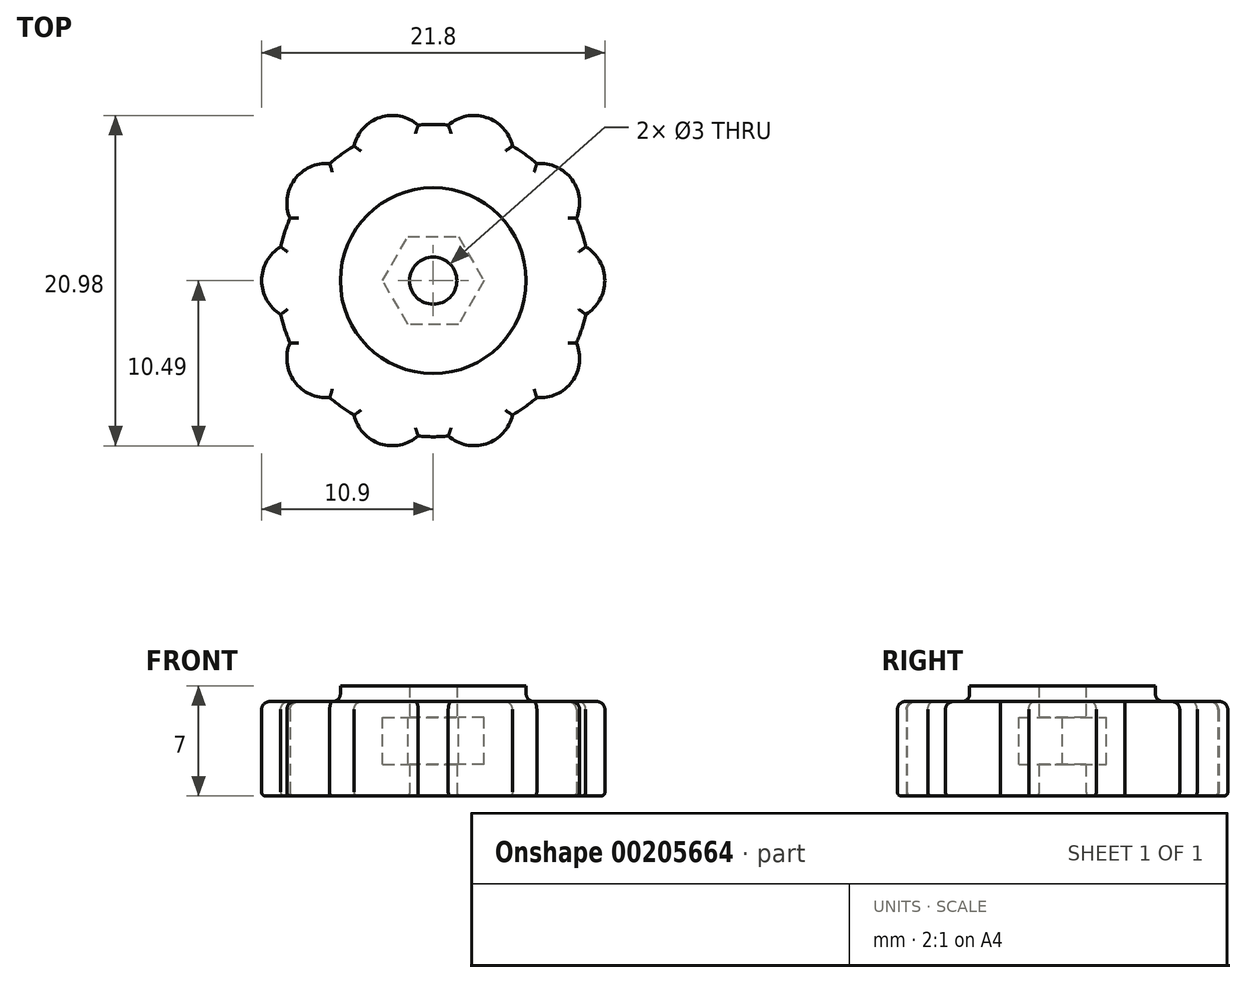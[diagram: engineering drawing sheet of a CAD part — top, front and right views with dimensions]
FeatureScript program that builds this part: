
annotation { "Feature Type Name" : "Feature", "Feature Type Description" : "" }
export const myFeature = defineFeature(function(context is Context, id is Id, definition is map)
    precondition{}
    {
        {
            var Q0;
            Q0=qCreatedBy(makeId("Top.planeOp"),FACE);
            var sketch = newSketch(context, id + "F0", { "sketchPlane" : qUnion([Q0])});
            skArc(sketch, "E0", {"start": v(-1.29, 2.14) * mm, "mid": v(-2.5, 0) * mm, "end": v(-1.29, -2.14) * mm});
            skArc(sketch, "E1.1.0", {"start": v(-0.7, -3.96) * mm, "mid": v(-0.42, -6.4) * mm, "end": v(1.82, -7.43) * mm});
            skArc(sketch, "E1.2.0", {"start": v(3.37, -8.55) * mm, "mid": v(5.03, -10.37) * mm, "end": v(7.45, -9.87) * mm});
            skArc(sketch, "E1.3.0", {"start": v(9.35, -9.87) * mm, "mid": v(11.77, -10.37) * mm, "end": v(13.43, -8.55) * mm});
            skArc(sketch, "E1.4.0", {"start": v(14.98, -7.43) * mm, "mid": v(17.22, -6.4) * mm, "end": v(17.5, -3.96) * mm});
            skArc(sketch, "E1.5.0", {"start": v(18.09, -2.14) * mm, "mid": v(19.3, 0) * mm, "end": v(18.09, 2.14) * mm});
            skArc(sketch, "E1.6.0", {"start": v(17.5, 3.96) * mm, "mid": v(17.22, 6.4) * mm, "end": v(14.98, 7.43) * mm});
            skArc(sketch, "E1.7.0", {"start": v(13.43, 8.55) * mm, "mid": v(11.77, 10.37) * mm, "end": v(9.35, 9.87) * mm});
            skArc(sketch, "E1.8.0", {"start": v(7.45, 9.87) * mm, "mid": v(5.03, 10.37) * mm, "end": v(3.37, 8.55) * mm});
            skArc(sketch, "E1.9.0", {"start": v(1.82, 7.43) * mm, "mid": v(-0.42, 6.4) * mm, "end": v(-0.7, 3.96) * mm});
            skPoint(sketch, "E1.center", {"position": v(8.4, 0) * mm});
            skArc(sketch, "E2", {"start": v(3.37, 8.55) * mm, "mid": v(2.57, 8.03) * mm, "end": v(1.82, 7.43) * mm});
            skCircle(sketch, "E3.cCircle", {"center": v(8.4, 0) * mm, "radius": 2.75 * mm, "construction": true});
            skLineSegment(sketch, "E3.0", {"start": v(9.99, -2.75) * mm, "end": v(6.81, -2.75) * mm});
            skLineSegment(sketch, "E3.1", {"start": v(6.81, -2.75) * mm, "end": v(5.22, 0) * mm});
            skLineSegment(sketch, "E3.2", {"start": v(5.22, 0) * mm, "end": v(6.81, 2.75) * mm});
            skLineSegment(sketch, "E3.3", {"start": v(6.81, 2.75) * mm, "end": v(9.99, 2.75) * mm});
            skLineSegment(sketch, "E3.4", {"start": v(9.99, 2.75) * mm, "end": v(11.58, 0) * mm});
            skLineSegment(sketch, "E3.5", {"start": v(11.58, 0) * mm, "end": v(9.99, -2.75) * mm});
            skPoint(sketch, "E3.0.midPoint", {"position": v(8.4, -2.75) * mm});
            skCircle(sketch, "E4", {"center": v(8.4, 0) * mm, "radius": 5.9 * mm});
            skArc(sketch, "E5.trimOffspring", {"start": v(-0.7, 3.96) * mm, "mid": v(-1.03, 3.07) * mm, "end": v(-1.29, 2.14) * mm});
            skArc(sketch, "E6.trimOffspring", {"start": v(-1.29, -2.14) * mm, "mid": v(-1.03, -3.07) * mm, "end": v(-0.7, -3.96) * mm});
            skArc(sketch, "E7.trimOffspring", {"start": v(1.82, -7.43) * mm, "mid": v(2.57, -8.03) * mm, "end": v(3.37, -8.55) * mm});
            skArc(sketch, "E8.trimOffspring", {"start": v(7.45, -9.87) * mm, "mid": v(8.4, -9.92) * mm, "end": v(9.35, -9.87) * mm});
            skArc(sketch, "E9.trimOffspring", {"start": v(17.5, -3.96) * mm, "mid": v(17.83, -3.07) * mm, "end": v(18.09, -2.14) * mm});
            skArc(sketch, "E10.trimOffspring", {"start": v(13.43, -8.55) * mm, "mid": v(14.23, -8.03) * mm, "end": v(14.98, -7.43) * mm});
            skArc(sketch, "E11.trimOffspring", {"start": v(18.09, 2.14) * mm, "mid": v(17.83, 3.07) * mm, "end": v(17.5, 3.96) * mm});
            skArc(sketch, "E12.trimOffspring", {"start": v(14.98, 7.43) * mm, "mid": v(14.23, 8.03) * mm, "end": v(13.43, 8.55) * mm});
            skArc(sketch, "E13.trimOffspring", {"start": v(9.35, 9.87) * mm, "mid": v(8.4, 9.92) * mm, "end": v(7.45, 9.87) * mm});
            skCircle(sketch, "E14", {"center": v(8.4, 0) * mm, "radius": 1.5 * mm});
            skSolve(sketch);
        }
        {
            var Q0;
            Q0=makeQuery(id+"F0.imprint","IMPRINT",FACE,{"disambiguationData":[TD([[makeQuery(id+"F0.imprint","IMPRINT",EDGE,{"derivedFrom":sQuery(id+"F0.wireOp",EDGE,"E0")}),1.0]])]});
            var Q1;
            Q1=makeQuery(id+"F0.imprint","IMPRINT",FACE,{"disambiguationData":[TD([[makeQuery(id+"F0.imprint","IMPRINT",EDGE,{"derivedFrom":sQuery(id+"F0.wireOp",EDGE,"E3.0")}),1.0]])]});
            var Q2;
            Q2=makeQuery(id+"F0.imprint","IMPRINT",FACE,{"disambiguationData":[TD([[makeQuery(id+"F0.imprint","IMPRINT",EDGE,{"derivedFrom":sQuery(id+"F0.wireOp",EDGE,"E3.0")}),-1.0]])]});
            extrude(context, id + "F1", {"entities" : qUnion([Q0, Q1, Q2]), "depth" : 6 * mm});
        }
        {
            var Q0;
            Q0=makeQuery(id+"F0.imprint","IMPRINT",FACE,{"disambiguationData":[TD([[makeQuery(id+"F0.imprint","IMPRINT",EDGE,{"derivedFrom":sQuery(id+"F0.wireOp",EDGE,"E3.0")}),1.0]])]});
            extrude(context, id + "F2", {"entities" : qUnion([Q0]), "operationType" : NewBodyOperationType.ADD, "depth" : 7 * mm});
        }
        {
            var Q0;
            Q0=makeQuery(id+"F0.imprint","IMPRINT",FACE,{"disambiguationData":[TD([[makeQuery(id+"F0.imprint","IMPRINT",EDGE,{"derivedFrom":sQuery(id+"F0.wireOp",EDGE,"E3.0")}),-1.0]])]});
            extrude(context, id + "F3", {"entities" : qUnion([Q0]), "operationType" : NewBodyOperationType.ADD, "depth" : 7 * mm});
        }
        {
            var Q0;
            {var subQ0=sQuery(id+"F0.wireOp",EDGE,"E3.5");var subQ1=sQuery(id+"F0.wireOp",EDGE,"E3.4");var subQ2=sQuery(id+"F0.wireOp",EDGE,"E3.3");var subQ3=sQuery(id+"F0.wireOp",EDGE,"E3.2");var subQ4=sQuery(id+"F0.wireOp",EDGE,"E3.1");var subQ5=sQuery(id+"F0.wireOp",EDGE,"E3.0");Q0=makeQuery(id+"F3.boolean.opBoolean","MERGE",FACE,{"derivedFrom":[makeQuery(id+"F2.opExtrude","CAP_FACE",FACE,{"disambiguationData":[OSD([subQ5,subQ4,subQ3,subQ2,subQ1,subQ0,sQuery(id+"F0.wireOp",EDGE,"E4")])],"isStart":false}),makeQuery(id+"F3.opExtrude","CAP_FACE",FACE,{"disambiguationData":[OSD([subQ5,subQ4,subQ3,subQ2,subQ1,subQ0,sQuery(id+"F0.wireOp",EDGE,"E14")])],"isStart":false})]});}
            var sketch = newSketch(context, id + "F4", { "sketchPlane" : qUnion([Q0])});
            skCircle(sketch, "E15.cCircle", {"center": v(8.4, 0) * mm, "radius": 2.79 * mm, "construction": true});
            skLineSegment(sketch, "E15.0", {"start": v(6.8, 2.79) * mm, "end": v(10, 2.79) * mm});
            skLineSegment(sketch, "E15.1", {"start": v(10, 2.79) * mm, "end": v(11.62, 0) * mm});
            skLineSegment(sketch, "E15.2", {"start": v(11.62, 0) * mm, "end": v(10, -2.79) * mm});
            skLineSegment(sketch, "E15.3", {"start": v(10, -2.79) * mm, "end": v(6.8, -2.79) * mm});
            skLineSegment(sketch, "E15.4", {"start": v(6.8, -2.79) * mm, "end": v(5.18, 0) * mm});
            skLineSegment(sketch, "E15.5", {"start": v(5.18, 0) * mm, "end": v(6.8, 2.79) * mm});
            skPoint(sketch, "E15.0.midPoint", {"position": v(8.4, 2.79) * mm});
            skSolve(sketch);
        }
        {
            var Q0;
            Q0=makeQuery(id+"F4.imprint","IMPRINT",FACE,{"disambiguationData":[TD([[makeQuery(id+"F4.imprint","IMPRINT",EDGE,{"derivedFrom":sQuery(id+"F4.wireOp",EDGE,"E15.0")}),-1.0]])]});
            extrude(context, id + "F5", {"entities" : qUnion([Q0]), "operationType" : NewBodyOperationType.REMOVE, "oppositeDirection" : true, "depth" : 5 * mm, "hasSecondDirection" : true, "secondDirectionOppositeDirection" : true, "secondDirectionDepth" : 2 * mm});
        }
        {
            var Q0;
            {var subQ0=sQuery(id+"F0.wireOp",EDGE,"E1.9.0");var subQ1=sQuery(id+"F0.wireOp",EDGE,"E10.trimOffspring");var subQ2=sQuery(id+"F0.wireOp",EDGE,"E1.7.0");var subQ3=sQuery(id+"F0.wireOp",EDGE,"E8.trimOffspring");var subQ4=sQuery(id+"F0.wireOp",EDGE,"E1.6.0");var subQ5=sQuery(id+"F0.wireOp",EDGE,"E1.5.0");var subQ6=sQuery(id+"F0.wireOp",EDGE,"E1.4.0");var subQ7=sQuery(id+"F0.wireOp",EDGE,"E0");var subQ8=sQuery(id+"F0.wireOp",EDGE,"E1.8.0");var subQ9=sQuery(id+"F0.wireOp",EDGE,"E9.trimOffspring");var subQ10=sQuery(id+"F0.wireOp",EDGE,"E1.1.0");var subQ11=sQuery(id+"F0.wireOp",EDGE,"E1.2.0");var subQ12=sQuery(id+"F0.wireOp",EDGE,"E1.3.0");var subQ13=sQuery(id+"F0.wireOp",EDGE,"E2");var subQ14=sQuery(id+"F0.wireOp",EDGE,"E5.trimOffspring");var subQ15=sQuery(id+"F0.wireOp",EDGE,"E11.trimOffspring");var subQ16=sQuery(id+"F0.wireOp",EDGE,"E12.trimOffspring");var subQ17=sQuery(id+"F0.wireOp",EDGE,"E6.trimOffspring");var subQ18=sQuery(id+"F0.wireOp",EDGE,"E13.trimOffspring");var subQ19=sQuery(id+"F0.wireOp",EDGE,"E7.trimOffspring");Q0=makeQuery(id+"F2.boolean.opBoolean","SPLIT",FACE,{"disambiguationData":[TD([makeQuery(id+"F1.opExtrude","SWEPT_FACE",FACE,{"disambiguationData":[OSD([subQ7])]})])],"derivedFrom":makeQuery(id+"F1.opExtrude","CAP_FACE",FACE,{"disambiguationData":[OSD([subQ7,subQ10,subQ11,subQ12,subQ6,subQ5,subQ4,subQ2,subQ8,subQ0,subQ13,subQ14,subQ17,subQ19,subQ3,subQ9,subQ1,subQ15,subQ16,subQ18,sQuery(id+"F0.wireOp",EDGE,"E14")])],"isStart":false})});}
            fillet(context, id + "F6", {"entities" : qUnion([Q0]), "radius" : 0.5 * mm, "tangentPropagation" : true, "allowEdgeOverflow" : false});
        }
        {
            var Q0;
            Q0=makeQuery(id+"F1.opExtrude","CAP_FACE",FACE,{"disambiguationData":[OSD([sQuery(id+"F0.wireOp",EDGE,"E0"),sQuery(id+"F0.wireOp",EDGE,"E1.1.0"),sQuery(id+"F0.wireOp",EDGE,"E1.2.0"),sQuery(id+"F0.wireOp",EDGE,"E1.3.0"),sQuery(id+"F0.wireOp",EDGE,"E1.4.0"),sQuery(id+"F0.wireOp",EDGE,"E1.5.0"),sQuery(id+"F0.wireOp",EDGE,"E1.6.0"),sQuery(id+"F0.wireOp",EDGE,"E1.7.0"),sQuery(id+"F0.wireOp",EDGE,"E1.8.0"),sQuery(id+"F0.wireOp",EDGE,"E1.9.0"),sQuery(id+"F0.wireOp",EDGE,"E2"),sQuery(id+"F0.wireOp",EDGE,"E5.trimOffspring"),sQuery(id+"F0.wireOp",EDGE,"E6.trimOffspring"),sQuery(id+"F0.wireOp",EDGE,"E7.trimOffspring"),sQuery(id+"F0.wireOp",EDGE,"E8.trimOffspring"),sQuery(id+"F0.wireOp",EDGE,"E9.trimOffspring"),sQuery(id+"F0.wireOp",EDGE,"E10.trimOffspring"),sQuery(id+"F0.wireOp",EDGE,"E11.trimOffspring"),sQuery(id+"F0.wireOp",EDGE,"E12.trimOffspring"),sQuery(id+"F0.wireOp",EDGE,"E13.trimOffspring"),sQuery(id+"F0.wireOp",EDGE,"E14")])],"isStart":true});
            fillet(context, id + "F7", {"entities" : qUnion([Q0]), "radius" : .25 * mm, "tangentPropagation" : true, "allowEdgeOverflow" : false});
        }
    });
